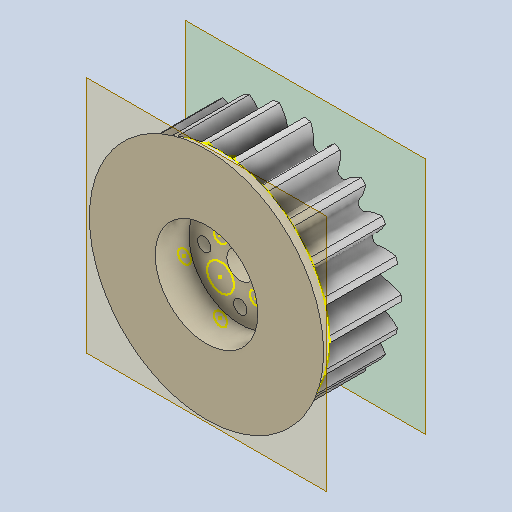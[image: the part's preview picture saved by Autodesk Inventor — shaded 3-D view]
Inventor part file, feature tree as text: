
AUTODESK INVENTOR PART (.ipt)
format: ipt  version: 2024.2 (Build 282272000, 272)  size: 402,432 bytes
history: native  units: mm
features: other x6, sketch x6
ambient origin geometry x8: Origin, YZ Plane, XZ Plane, XY Plane, X Axis, Y Axis, Z Axis, Center Point
bodies: Body1 (feature_tree)
feature tree (12):
  other  "Шест_MIR.ipt"
  other  "Твердое тело1::Шест_MIR.ipt"
  other  "Элемент создания тегов1"
  sketch  "Sketch1"  dims[d0=10.0mm]
  sketch  "Эскиз2"
  sketch  "Эскиз3"
  sketch  "Эскиз4"
  sketch  "Эскиз5"
  sketch  "Эскиз6"
  other  "РабПлоскость1"
  other  "РабПлоскость2"
  other  "Твердое тело1"
